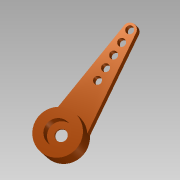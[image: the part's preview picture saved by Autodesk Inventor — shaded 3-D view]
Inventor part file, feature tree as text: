
AUTODESK INVENTOR PART (.ipt)
format: ipt  version: 2015 SP1 (Build 190203100, 203)  size: 126,976 bytes
history: native  units: mm
features: extrude x4, sketch x3, projected_geometry x1
ambient origin geometry x8: Origin, YZ Plane, XZ Plane, XY Plane, X Axis, Y Axis, Z Axis, Center Point
bodies: Solid1 (feature_tree)
feature tree (8):
  sketch  "Sketch1"  dims[d2=2.22mm d3=0.629449mm]
  extrude  "Extrusion1"  Depth=0.629449mm
  extrude  "Extrusion2"  Depth=0.63mm TaperAngle=0.0deg
  extrude  "Extrusion3"  Depth=2.06mm
  extrude  "Extrusion4"  Depth=2.06mm
  sketch  "Sketch2"  dims[d4=2.07mm d5=0.0mm d6=0.63mm d7=0.0mm]
  projected_geometry  "Projected Loop1"
  sketch  "Sketch3"  dims[d8=2.81mm d9=0.0mm d14=1.5mm d15=0.46mm d16=1.5mm d17=0.95mm d18=1.5mm d19=1.5mm d20=1.5mm d21=0.95mm d22=0.95mm d23=0.95mm d24=2.06mm d25=0.0mm d26=4.75mm]
